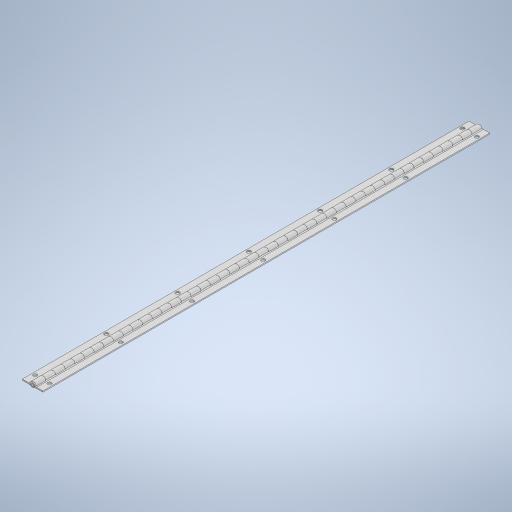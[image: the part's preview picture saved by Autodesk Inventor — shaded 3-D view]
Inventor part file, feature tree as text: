
AUTODESK INVENTOR PART (.ipt)
format: ipt  version: 2023 (Build 270158000, 158)  size: 603,648 bytes
history: native  units: in
note: dims shown in document units (in); Inventor stores cm internally (conversion verified against a paired STEP export)
features: extrude x2, sketch x2, other x2, hole x1, pattern_linear x1
ambient origin geometry x8: Origin, YZ Plane, XZ Plane, XY Plane, X Axis, Y Axis, Z Axis, Center Point
bodies: Solid1 (feature_tree), Solid2 (feature_tree), Solid3 (feature_tree)
feature tree (8):
  extrude  "Extrusion2"  TaperAngle=0.0deg  [1 undecoded]
  hole  "Hole1"  [1 undecoded]
  pattern_linear  "Rectangular Pattern1"  Spacing1=0.7385in  [1 undecoded]
  sketch  "Sketch2"  dims[d2=12.9469in d3=0.0in d4=0.0in]
  sketch  "Sketch3"  dims[d5=0.194in d6=0.75in d7=0.375in d8=0.25in d9=0.5635in d10=1.0in d11=0.8108in d13=0.162in d15=0.7385in d16=0.5in d17=2.7559in d19=3.6755in]
  other  "LPattern1"
  other  "LPattern2"
  extrude  "Extrude5"  Depth=0.5in
note: 3 required parameter values undecoded (feature->parameter linkage not recoverable at this tier; creation-order binding heuristic only, values carry confidence <= 0.55)
